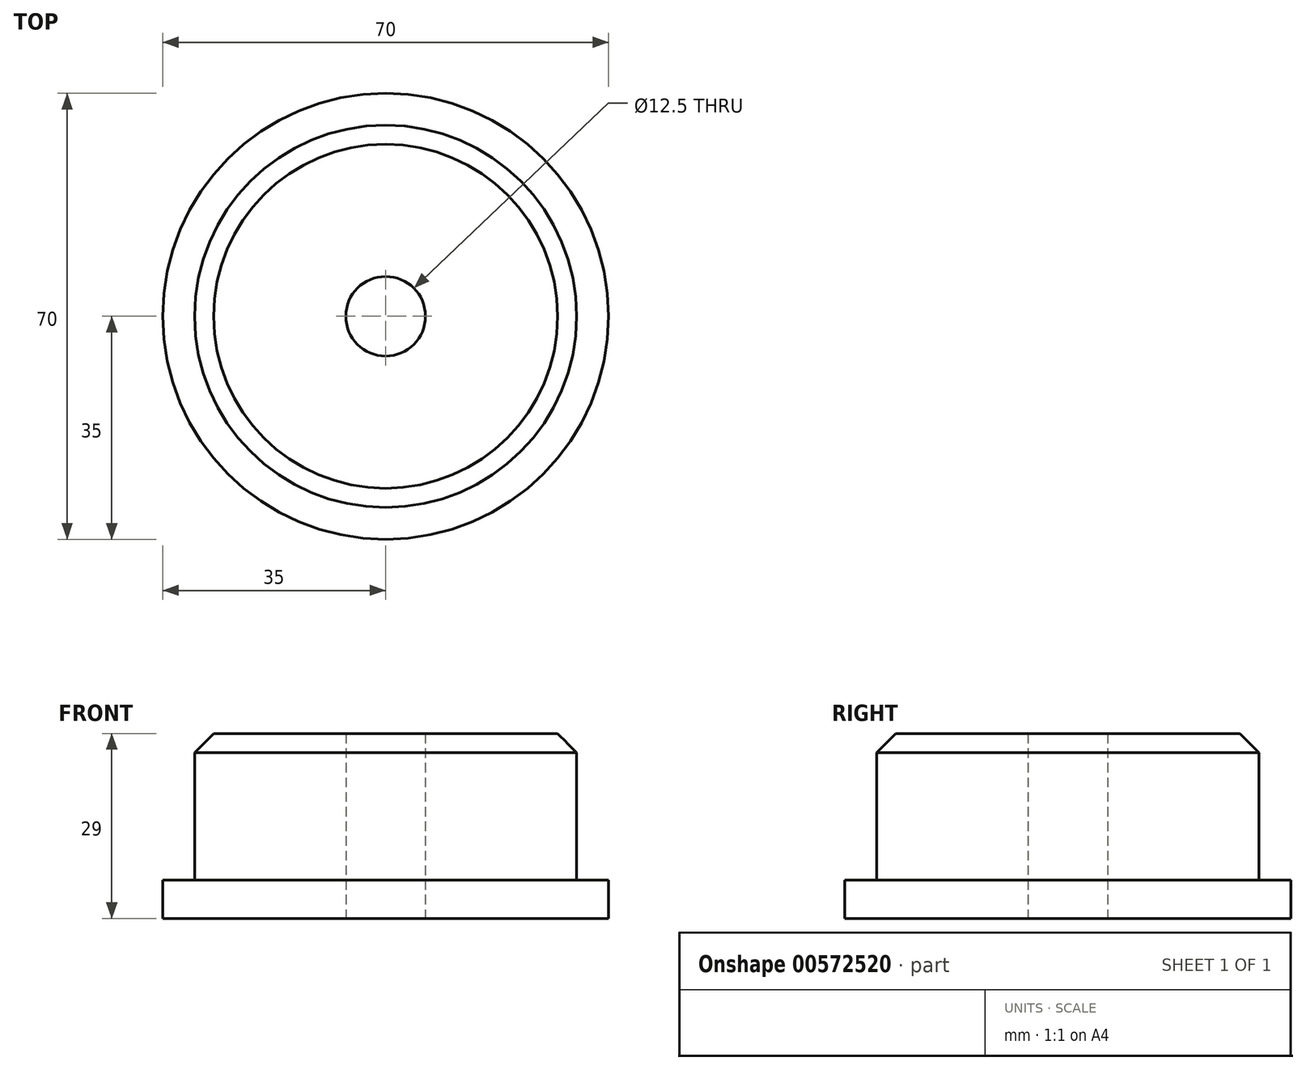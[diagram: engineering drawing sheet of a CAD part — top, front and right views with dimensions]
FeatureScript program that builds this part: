
annotation { "Feature Type Name" : "Feature", "Feature Type Description" : "" }
export const myFeature = defineFeature(function(context is Context, id is Id, definition is map)
    precondition{}
    {
        {
            var Q0;
            Q0=qCreatedBy(makeId("Top.planeOp"),FACE);
            var sketch = newSketch(context, id + "F0", { "sketchPlane" : qUnion([Q0])});
            skCircle(sketch, "E0", {"center": v(0, 0) * mm, "radius": 35 * mm});
            skCircle(sketch, "E1", {"center": v(0, 0) * mm, "radius": 30 * mm});
            skCircle(sketch, "E2", {"center": v(0, 0) * mm, "radius": 6.25 * mm});
            skSolve(sketch);
        }
        {
            var Q0;
            Q0=makeQuery(id+"F0.imprint","IMPRINT",FACE,{"disambiguationData":[TD([[makeQuery(id+"F0.imprint","IMPRINT",EDGE,{"derivedFrom":sQuery(id+"F0.wireOp",EDGE,"E1")}),1.0]])]});
            extrude(context, id + "F1", {"entities" : qUnion([Q0]), "depth" : 29 * mm, "offsetDistance" : 25 * mm});
        }
        {
            var Q0;
            Q0=qCreatedBy(makeId("Top.planeOp"),FACE);
            var sketch = newSketch(context, id + "F2", { "sketchPlane" : qUnion([Q0])});
            skCircle(sketch, "E3", {"center": v(0, 0) * mm, "radius": 35 * mm});
            skCircle(sketch, "E4", {"center": v(0, 0) * mm, "radius": 6.25 * mm});
            skSolve(sketch);
        }
        {
            var Q0;
            Q0 = qSketchRegion(id + "F2", true);
            extrude(context, id + "F3", {"entities" : qUnion([Q0]), "operationType" : NewBodyOperationType.ADD, "depth" : 6 * mm, "offsetDistance" : 25 * mm});
        }
        {
            var Q0;
            Q0=makeQuery(id+"F1.opExtrude","CAP_EDGE",EDGE,{"disambiguationData":[OSD([sQuery(id+"F0.wireOp",EDGE,"E1")])],"isStart":false});
            chamfer(context, id + "F4", {"entities" : qUnion([Q0]), "width" : 3 * mm, "tangentPropagation" : true});
        }
    });
